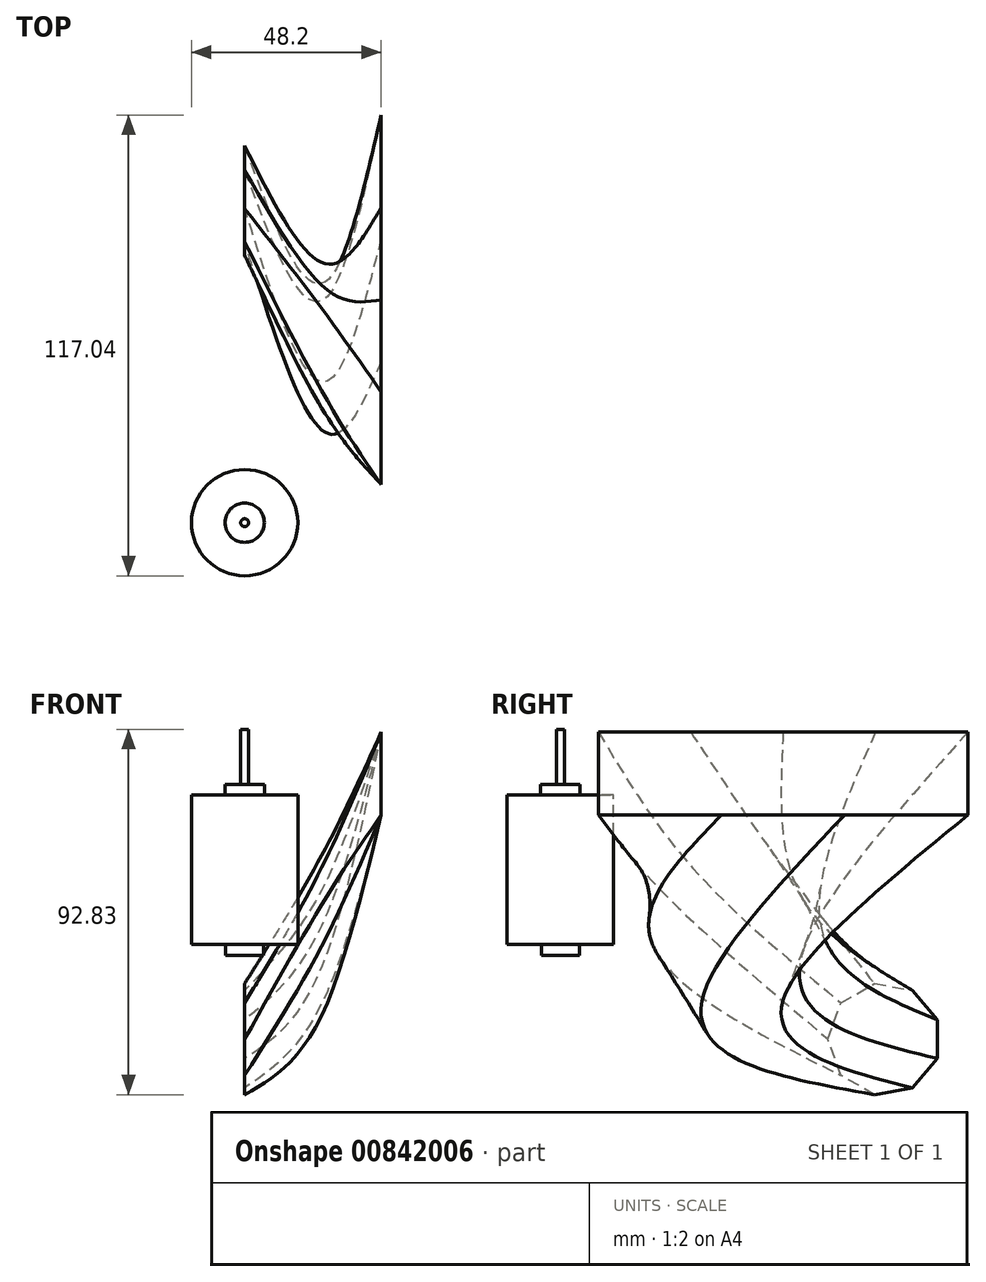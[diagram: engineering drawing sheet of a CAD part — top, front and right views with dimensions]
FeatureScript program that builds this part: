
annotation { "Feature Type Name" : "Feature", "Feature Type Description" : "" }
export const myFeature = defineFeature(function(context is Context, id is Id, definition is map)
    precondition{}
    {
        {
            var Q0;
            Q0=qCreatedBy(makeId("Right.planeOp"),FACE);
            var sketch = newSketch(context, id + "F0", { "sketchPlane" : qUnion([Q0])});
            skLineSegment(sketch, "E0", {"start": v(-61.6, 44.69) * mm, "end": v(-61.6, -12.71) * mm});
            skLineSegment(sketch, "E1", {"start": v(-61.6, -12.71) * mm, "end": v(-56.8, -12.71) * mm});
            skLineSegment(sketch, "E2", {"start": v(-56.8, -12.71) * mm, "end": v(-56.8, -10.01) * mm});
            skLineSegment(sketch, "E3", {"start": v(-56.8, -10.01) * mm, "end": v(-48.1, -10.01) * mm});
            skLineSegment(sketch, "E4", {"start": v(-48.1, -10.01) * mm, "end": v(-48.1, 27.99) * mm});
            skLineSegment(sketch, "E5", {"start": v(-48.1, 27.99) * mm, "end": v(-56.6, 27.99) * mm});
            skLineSegment(sketch, "E6", {"start": v(-56.6, 27.99) * mm, "end": v(-56.6, 30.69) * mm});
            skLineSegment(sketch, "E7", {"start": v(-56.6, 30.69) * mm, "end": v(-60.6, 30.69) * mm});
            skLineSegment(sketch, "E8", {"start": v(-60.6, 30.69) * mm, "end": v(-60.6, 44.69) * mm});
            skLineSegment(sketch, "E9", {"start": v(-60.6, 44.69) * mm, "end": v(-61.6, 44.69) * mm});
            skSolve(sketch);
        }
        {
            var Q0;
            Q0=makeQuery(id+"F0.imprint","IMPRINT",FACE,{"disambiguationData":[TD([[makeQuery(id+"F0.imprint","IMPRINT",EDGE,{"derivedFrom":sQuery(id+"F0.wireOp",EDGE,"E0")}),1.0]])]});
            var Q1;
            Q1=sQuery(id+"F0.wireOp",EDGE,"E0");
            revolve(context, id + "F1", {"surfaceOperationType" : NewSurfaceOperationType.NEW, "entities" : qUnion([Q0]), "axis" : qUnion([Q1]), "revolveType" : RevolveType.FULL});
        }
        {
            var Q0;
            Q0=qCreatedBy(makeId("Right.planeOp"),FACE);
            cPlane(context, id + "F2", {"entities" : qUnion([Q0]), "cplaneType" : CPlaneType.OFFSET, "offset" : 34.7 * mm, "width" : 150 * mm, "height" : 150 * mm});
        }
        {
            var Q0;
            Q0=qCreatedBy(makeId("Right.planeOp"),FACE);
            cPlane(context, id + "F3", {"entities" : qUnion([Q0]), "cplaneType" : CPlaneType.OFFSET, "offset" : 21 * mm, "width" : 150 * mm, "height" : 150 * mm});
        }
        {
            var Q0;
            Q0=qCreatedBy(id+"F2.planeOp",FACE);
            var sketch = newSketch(context, id + "F4", { "sketchPlane" : qUnion([Q0])});
            skLineSegment(sketch, "E10.bottom", {"start": v(-51.91, 43.99) * mm, "end": v(41.95, 43.99) * mm});
            skLineSegment(sketch, "E10.top", {"start": v(-51.91, 22.93) * mm, "end": v(41.95, 22.93) * mm});
            skLineSegment(sketch, "E10.left", {"start": v(-51.91, 43.99) * mm, "end": v(-51.91, 22.93) * mm});
            skLineSegment(sketch, "E10.right", {"start": v(41.95, 43.99) * mm, "end": v(41.95, 22.93) * mm});
            skSolve(sketch);
        }
        {
            var Q0;
            Q0=qCreatedBy(id+"F3.planeOp",FACE);
            var sketch = newSketch(context, id + "F5", { "sketchPlane" : qUnion([Q0])});
            skCircle(sketch, "E11.cCircle", {"center": v(-17.38, -4.72) * mm, "radius": 18.8 * mm, "construction": true});
            skLineSegment(sketch, "E11.0", {"start": v(4.14, -1.87) * mm, "end": v(-4.14, -21.93) * mm});
            skLineSegment(sketch, "E11.1", {"start": v(-4.14, -21.93) * mm, "end": v(-25.67, -24.79) * mm});
            skLineSegment(sketch, "E11.2", {"start": v(-25.67, -24.79) * mm, "end": v(-38.9, -7.58) * mm});
            skLineSegment(sketch, "E11.3", {"start": v(-38.9, -7.58) * mm, "end": v(-30.61, 12.49) * mm});
            skLineSegment(sketch, "E11.4", {"start": v(-30.61, 12.49) * mm, "end": v(-9.1, 15.35) * mm});
            skLineSegment(sketch, "E11.5", {"start": v(-9.1, 15.35) * mm, "end": v(4.14, -1.87) * mm});
            skPoint(sketch, "E11.0.midPoint", {"position": v(0, -11.9) * mm});
            skSolve(sketch);
        }
        {
            var Q0;
            Q0=qCreatedBy(makeId("Right.planeOp"),FACE);
            var sketch = newSketch(context, id + "F6", { "sketchPlane" : qUnion([Q0])});
            skCircle(sketch, "E12.cCircle", {"center": v(20.7, -34.02) * mm, "radius": 13.47 * mm, "construction": true});
            skLineSegment(sketch, "E12.0", {"start": v(34.16, -29.12) * mm, "end": v(34.16, -38.92) * mm});
            skLineSegment(sketch, "E12.1", {"start": v(34.16, -38.92) * mm, "end": v(27.86, -46.43) * mm});
            skLineSegment(sketch, "E12.2", {"start": v(27.86, -46.43) * mm, "end": v(18.2, -48.14) * mm});
            skLineSegment(sketch, "E12.3", {"start": v(18.2, -48.14) * mm, "end": v(9.71, -43.23) * mm});
            skLineSegment(sketch, "E12.4", {"start": v(9.71, -43.23) * mm, "end": v(6.36, -34.02) * mm});
            skLineSegment(sketch, "E12.5", {"start": v(6.36, -34.02) * mm, "end": v(9.71, -24.81) * mm});
            skLineSegment(sketch, "E12.6", {"start": v(9.71, -24.81) * mm, "end": v(18.2, -19.9) * mm});
            skLineSegment(sketch, "E12.7", {"start": v(18.2, -19.9) * mm, "end": v(27.86, -21.61) * mm});
            skLineSegment(sketch, "E12.8", {"start": v(27.86, -21.61) * mm, "end": v(34.16, -29.12) * mm});
            skPoint(sketch, "E12.0.midPoint", {"position": v(34.16, -34.02) * mm});
            skSolve(sketch);
        }
        {
            var Q0;
            Q0=makeQuery(id+"F4.imprint","IMPRINT",FACE,{"disambiguationData":[TD([[makeQuery(id+"F4.imprint","IMPRINT",EDGE,{"derivedFrom":sQuery(id+"F4.wireOp",EDGE,"E10.bottom")}),-1.0]])]});
            var Q1;
            Q1=makeQuery(id+"F5.imprint","IMPRINT",FACE,{"disambiguationData":[TD([[makeQuery(id+"F5.imprint","IMPRINT",EDGE,{"derivedFrom":sQuery(id+"F5.wireOp",EDGE,"E11.0")}),-1.0]])]});
            var Q2;
            Q2=makeQuery(id+"F6.imprint","IMPRINT",FACE,{"disambiguationData":[TD([[makeQuery(id+"F6.imprint","IMPRINT",EDGE,{"derivedFrom":sQuery(id+"F6.wireOp",EDGE,"E12.0")}),-1.0]])]});
            loft(context, id + "F7", {"sheetProfilesArray" : [{ "sheetProfileEntities" : qUnion([Q0]) }, { "sheetProfileEntities" : qUnion([Q1]) }, { "sheetProfileEntities" : qUnion([Q2]) }]});
        }
    });
